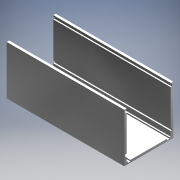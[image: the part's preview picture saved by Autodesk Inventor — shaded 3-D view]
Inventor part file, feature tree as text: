
AUTODESK INVENTOR PART (.ipt)
format: ipt  version: 2019 (Build 230136000, 136)  size: 141,312 bytes
history: native  units: in
note: dims shown in document units (in); Inventor stores cm internally (conversion verified against a paired STEP export)
features: extrude x1, sketch x1
ambient origin geometry x8: Origin, YZ Plane, XZ Plane, XY Plane, X Axis, Y Axis, Z Axis, Center Point
bodies: Solid1 (feature_tree)
feature tree (2):
  extrude  "Extrusion1"  Depth=5.0in
  sketch  "Sketch1"  dims[d0=5.0in d1=5.0in d2=0.25in d3=4.75in d4=4.5in d5=0.125in d9=0.125in d10=0.125in d11=0.125in d12=0.25in d13=0.125in d14=0.125in d15=0.25in d16=0.125in d17=0.125in d18=0.25in d19=12.0in d20=0.0in d21=0.5in d22=0.125in d23=0.25in d24=0.5in d25=0.125in d26=0.25in]
